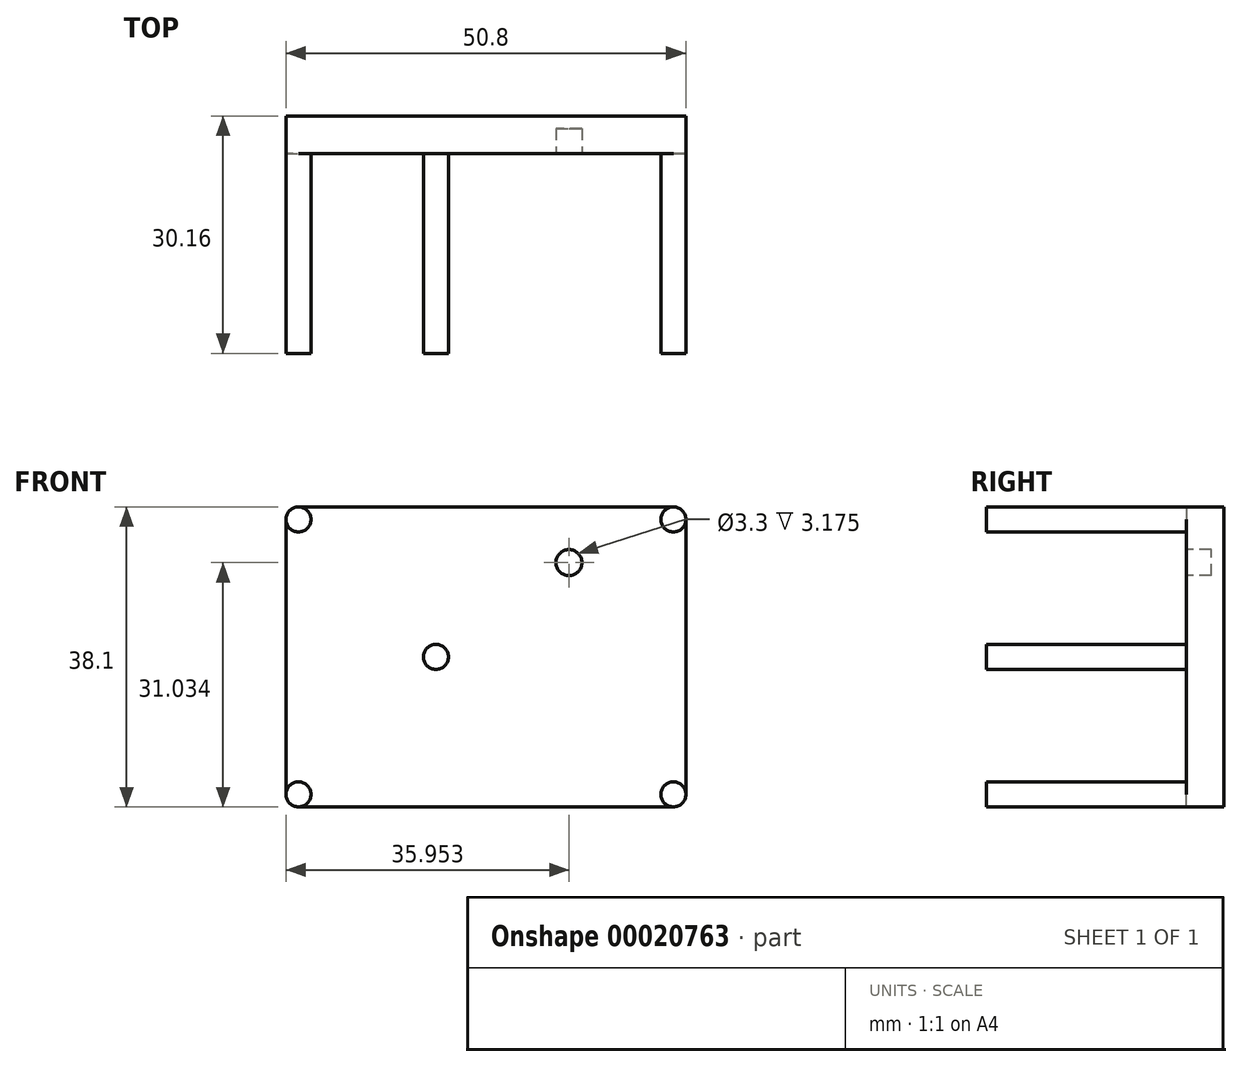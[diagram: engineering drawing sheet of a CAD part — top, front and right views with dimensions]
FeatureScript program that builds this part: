
annotation { "Feature Type Name" : "Feature", "Feature Type Description" : "" }
export const myFeature = defineFeature(function(context is Context, id is Id, definition is map)
    precondition{}
    {
        {
            var Q0;
            Q0=qCreatedBy(makeId("Front.planeOp"),FACE);
            var sketch = newSketch(context, id + "F0", { "sketchPlane" : qUnion([Q0])});
            skLineSegment(sketch, "E0.bottom", {"start": v(-23.81, 19.05) * mm, "end": v(23.81, 19.05) * mm});
            skLineSegment(sketch, "E0.top", {"start": v(-23.81, -19.05) * mm, "end": v(23.81, -19.05) * mm});
            skLineSegment(sketch, "E0.left", {"start": v(-25.4, 17.46) * mm, "end": v(-25.4, -17.46) * mm});
            skLineSegment(sketch, "E0.right", {"start": v(25.4, 17.46) * mm, "end": v(25.4, -17.46) * mm});
            skPoint(sketch, "E1", {"position": v(-25.4, 0) * mm});
            skPoint(sketch, "E2", {"position": v(0, 19.05) * mm});
            skPoint(sketch, "E3.visualSharp", {"position": v(-25.4, 19.05) * mm});
            skArc(sketch, "E3.filletArc", {"start": v(-23.81, 19.05) * mm, "mid": v(-24.94, 18.59) * mm, "end": v(-25.4, 17.46) * mm});
            skPoint(sketch, "E4.visualSharp", {"position": v(25.4, 19.05) * mm});
            skArc(sketch, "E4.filletArc", {"start": v(25.4, 17.46) * mm, "mid": v(24.94, 18.59) * mm, "end": v(23.81, 19.05) * mm});
            skPoint(sketch, "E5.visualSharp", {"position": v(25.4, -19.05) * mm});
            skArc(sketch, "E5.filletArc", {"start": v(23.81, -19.05) * mm, "mid": v(24.94, -18.59) * mm, "end": v(25.4, -17.46) * mm});
            skPoint(sketch, "E6.visualSharp", {"position": v(-25.4, -19.05) * mm});
            skArc(sketch, "E6.filletArc", {"start": v(-25.4, -17.46) * mm, "mid": v(-24.94, -18.59) * mm, "end": v(-23.81, -19.05) * mm});
            skSolve(sketch);
        }
        {
            var Q0;
            Q0=makeQuery(id+"F0.imprint","IMPRINT",FACE,{"disambiguationData":[TD([[makeQuery(id+"F0.imprint","IMPRINT",EDGE,{"derivedFrom":sQuery(id+"F0.wireOp",EDGE,"E0.bottom")}),-1.0]])]});
            extrude(context, id + "F1", {"entities" : qUnion([Q0]), "oppositeDirection" : true, "depth" : 4.76 * mm});
        }
        {
            var Q0;
            Q0=makeQuery(id+"F1.opExtrude","CAP_FACE",FACE,{"disambiguationData":[OSD([sQuery(id+"F0.wireOp",EDGE,"E0.bottom"),sQuery(id+"F0.wireOp",EDGE,"E0.top"),sQuery(id+"F0.wireOp",EDGE,"E0.left"),sQuery(id+"F0.wireOp",EDGE,"E0.right")])],"isStart":true});
            var sketch = newSketch(context, id + "F2", { "sketchPlane" : qUnion([Q0])});
            skLineSegment(sketch, "E7.0", {"start": v(-23.81, 19.05) * mm, "end": v(-23.81, 19.05) * mm});
            skCircle(sketch, "E8", {"center": v(-6.35, 0) * mm, "radius": 1.59 * mm});
            skSolve(sketch);
        }
        {
            var Q0;
            Q0=makeQuery(id+"F2.imprint","IMPRINT",FACE,{"disambiguationData":[TD([[makeQuery(id+"F2.imprint","IMPRINT",EDGE,{"derivedFrom":sQuery(id+"F2.wireOp",EDGE,"E8")}),1.0]])]});
            extrude(context, id + "F3", {"entities" : qUnion([Q0]), "operationType" : NewBodyOperationType.ADD, "depth" : 25.4 * mm});
        }
        {
            var Q0;
            Q0=makeQuery(id+"F1.opExtrude","CAP_FACE",FACE,{"disambiguationData":[OSD([sQuery(id+"F0.wireOp",EDGE,"E0.bottom"),sQuery(id+"F0.wireOp",EDGE,"E0.top"),sQuery(id+"F0.wireOp",EDGE,"E0.left"),sQuery(id+"F0.wireOp",EDGE,"E0.right"),sQuery(id+"F0.wireOp",EDGE,"E3.filletArc"),sQuery(id+"F0.wireOp",EDGE,"E4.filletArc"),sQuery(id+"F0.wireOp",EDGE,"E5.filletArc"),sQuery(id+"F0.wireOp",EDGE,"E6.filletArc")])],"isStart":true});
            var sketch = newSketch(context, id + "F4", { "sketchPlane" : qUnion([Q0])});
            skCircle(sketch, "E9", {"center": v(-23.81, 17.46) * mm, "radius": 1.59 * mm});
            skCircle(sketch, "E10", {"center": v(23.81, 17.46) * mm, "radius": 1.59 * mm});
            skCircle(sketch, "E11", {"center": v(-23.81, -17.46) * mm, "radius": 1.59 * mm});
            skCircle(sketch, "E12", {"center": v(23.81, -17.46) * mm, "radius": 1.59 * mm});
            skSolve(sketch);
        }
        {
            var Q0;
            Q0 = qSketchRegion(id + "F4", true);
            extrude(context, id + "F5", {"entities" : qUnion([Q0]), "operationType" : NewBodyOperationType.ADD, "depth" : 25.4 * mm});
        }
        {
            var Q0;
            Q0=makeQuery(id+"F1.opExtrude","CAP_FACE",FACE,{"disambiguationData":[OSD([sQuery(id+"F0.wireOp",EDGE,"E0.bottom"),sQuery(id+"F0.wireOp",EDGE,"E0.top"),sQuery(id+"F0.wireOp",EDGE,"E0.left"),sQuery(id+"F0.wireOp",EDGE,"E0.right"),sQuery(id+"F0.wireOp",EDGE,"E3.filletArc"),sQuery(id+"F0.wireOp",EDGE,"E4.filletArc"),sQuery(id+"F0.wireOp",EDGE,"E5.filletArc"),sQuery(id+"F0.wireOp",EDGE,"E6.filletArc")])],"isStart":true});
            var sketch = newSketch(context, id + "F6", { "sketchPlane" : qUnion([Q0])});
            skCircle(sketch, "E13", {"center": v(-6.35, 0) * mm, "radius": 12.7 * mm});
            skCircle(sketch, "E14", {"center": v(10.55, 11.98) * mm, "radius": 12.7 * mm});
            skPoint(sketch, "E15", {"position": v(6.35, 0) * mm});
            skPoint(sketch, "E16", {"position": v(0, 19.05) * mm});
            skCircle(sketch, "E17", {"center": v(10.55, 11.98) * mm, "radius": 1.65 * mm});
            skSolve(sketch);
        }
        {
            var Q0;
            Q0=makeQuery(id+"F6.imprint","IMPRINT",FACE,{"disambiguationData":[TD([[makeQuery(id+"F6.imprint","IMPRINT",EDGE,{"derivedFrom":sQuery(id+"F6.wireOp",EDGE,"E17")}),1.0]])]});
            extrude(context, id + "F7", {"entities" : qUnion([Q0]), "operationType" : NewBodyOperationType.REMOVE, "oppositeDirection" : true, "depth" : 3.17 * mm});
        }
    });
